# Revit family: 11Landscaping_Bike-Racks-Shelters_Saris-Infrastructure_Wall-Mounted-Public-Work-Stand
name_source: partatom
category: Site
units: mm (PartAtom-declared; Revit-internal decimal feet)

## family parameters
Cut with Voids When Loaded = No
Host = Face
OmniClass Number = 23.40.10.11.11
Part Type = Normal
Round Connector Dimension = Use Diameter
Shared = No

## types (2) — shared parameters
Date Updated = 2025/03/14
Default Elevation = 48.00"
Height = 61.00"
Length = 16.00"
Manufacturer = Saris Infrastructure
Product Documentation Link = https://cdn.shopify.com
Product Page URL = https://sarisinfrastructure.com
Product Specifications = • Designed for indoor or outdoor use  • Wall mount design; small footprint is perfect for small spaces  • Can be mounted to posts using U-bolt holes in back panel slots  • Pairs perfectly with Saris Bike Pumps  • Tools securely attached by braided stainless steel cables
Product data url = https://bimobject.com
URL = https://www.sarisinfrastructure.com
Version = 1
Warranty = 2 years
Weight = 29.00 lbf
Width = 11.00"

## per-type parameters (varying)
| type | Description | Model | Product Material |
| Wall Mounted Public Work Stand - Powder Coat - Black | Wall Mounted Public Work Stand, Powder Coat - Black - 29755BLK | 29755BLK | Saris Infrastructure - Mild Steel - Powder Coat - Black |
| Wall Mounted Public Work Stand - Powder Coat - Red | Wall Mounted Public Work Stand, Powder Coat - Red - 29755RED | 29755RED | Saris Infrastructure - Mild Steel - Powder Coat - Red |

## geometry (parser evidence)
native form markers: Sweep x2
no freeform markers — native parametric forms only
